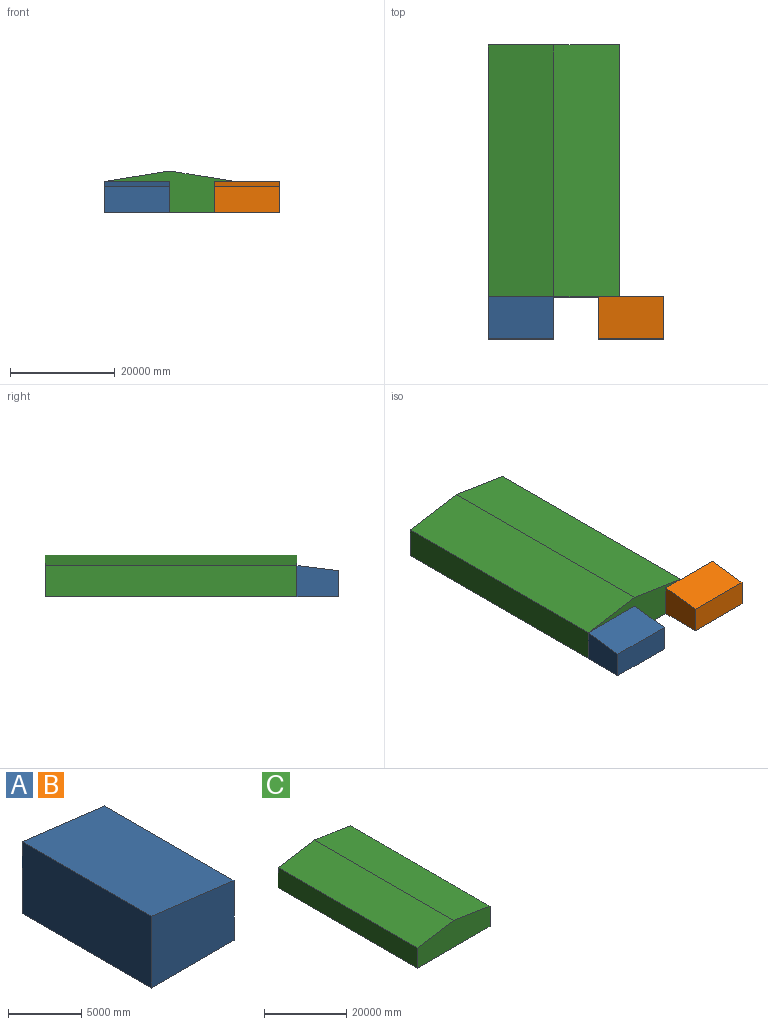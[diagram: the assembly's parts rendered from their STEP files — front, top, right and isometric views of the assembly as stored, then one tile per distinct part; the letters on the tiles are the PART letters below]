
ASSEMBLY  parts=3 mates=2
PART A: 6 faces, bbox 8000x12500x6000 mm
  f0: plane 12500x6000mm, normal (-1,0,0), area 75000000mm2, adj f1,f3,f4,f5
  f1: plane 12500x8000mm, normal (0,0,-1), area 100000000mm2, adj f0,f2,f4,f5
  f2: plane 12500x5000mm, normal (1,0,0), area 62500000mm2, adj f1,f3,f4,f5
  f3: plane 12500x8000mm, normal (0.12,0,0.99), area 100778221.9mm2, adj f0,f2,f4,f5
  f4: plane 8000x6000mm, normal (0,1,0), area 44000000mm2, adj f0,f1,f2,f3
  f5: plane 8000x6000mm, normal (0,-1,0), area 44000000mm2, adj f0,f1,f2,f3
PART B: same geometry as A
PART C: 7 faces, bbox 25000x48000x8000 mm
  f0: plane 48000x6000mm, normal (-1,0,0), area 288000000mm2, adj f1,f4,f5,f6
  f1: plane 48000x25000mm, normal (0,0,-1), area 1200000000mm2, adj f0,f2,f5,f6
  f2: plane 48000x6000mm, normal (1,0,0), area 288000000mm2, adj f1,f3,f5,f6
  f3: plane 48000x12500mm, normal (0.16,0,0.99), area 607631467.3mm2, adj f2,f4,f5,f6
  f4: plane 48000x12500mm, normal (-0.16,0,0.99), area 607631467.3mm2, adj f0,f3,f5,f6
  f5: plane 25000x8000mm, normal (0,1,0), area 175000000mm2, adj f0,f1,f2,f3,f4
  f6: plane 25000x8000mm, normal (0,-1,0), area 175000000mm2, adj f0,f1,f2,f3,f4
PLACE A rot(axis=(0,0,-1),90deg) t=(-12526.53,-24022.59,-4010.91)mm
PLACE B rot(axis=(0,0,-1),90deg) t=(8412.46,-24022.59,-4010.91)mm
PLACE C t=(-12526.53,-24022.59,-4010.91)mm fixed
MATE fastened C.f1 <-> A.f1  axis (0,0,1) through (-12526.53,-24022.59,-4010.91)mm
MATE slider C.f2 <-> B.f4  axis (-1,0,0) through (12473.47,-24022.59,-4010.91)mm
